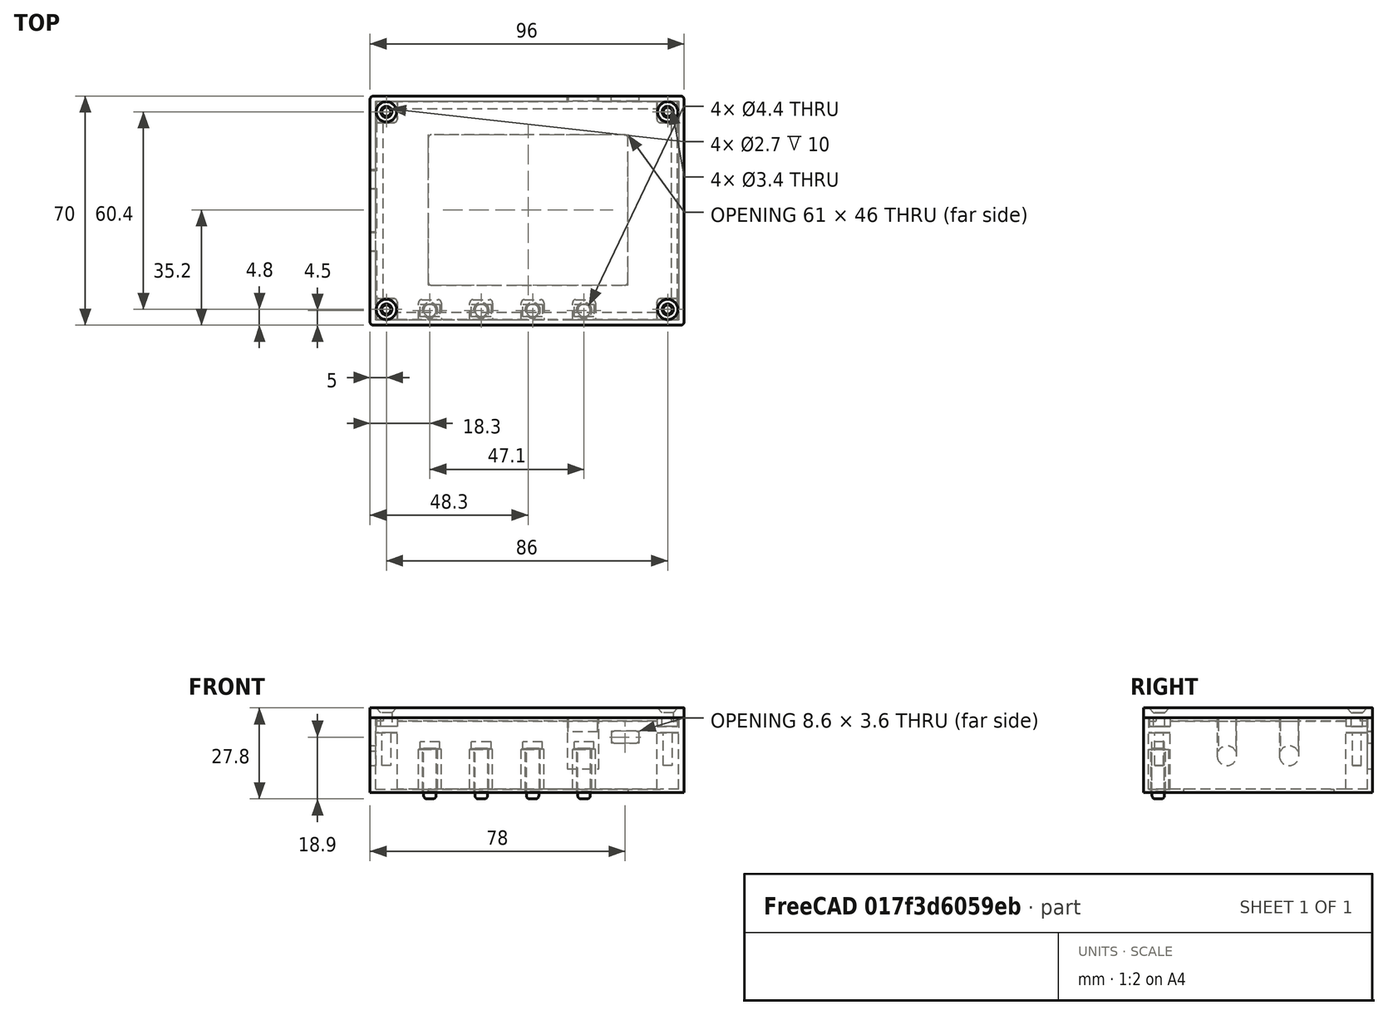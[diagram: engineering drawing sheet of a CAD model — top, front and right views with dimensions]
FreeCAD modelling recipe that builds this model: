
FCSTD DOCUMENT  (FreeCAD 0.18R16131 (Git))
Label: SigGen_Housing
License: All rights reserved
LicenseURL: http://en.wikipedia.org/wiki/All_rights_reserved
objects: Sketcher::SketchObject×35, PartDesign::Pad×18, PartDesign::Pocket×17, PartDesign::Fillet×10, PartDesign::Body×6, Mesh::Feature×3, PartDesign::Chamfer×2, Spreadsheet::Sheet×1
note: 123 computed .brp shape members not serialized (recipe doc carries the construction recipe); baked Part::Feature solids carry a one-line shape summary decoded from their .brp

FEATURE [Sketcher::SketchObject] Sketch
  MapMode = 5
  Support = -> [XY_Plane]
  expr: Constraints[11] = Constraints.OWidth / 2
  expr: Constraints[10] = Constraints.OLength / 2
  expr: Constraints.OWidth = Measures.B2
  expr: Constraints.OLength = Measures.A2
  sketch-geometry (4):
    g0: LineSegment StartX=-48 StartY=35 StartZ=0 EndX=48 EndY=35 EndZ=0
    g1: LineSegment StartX=48 StartY=35 StartZ=0 EndX=48 EndY=-35 EndZ=0
    g2: LineSegment StartX=48 StartY=-35 StartZ=0 EndX=-48 EndY=-35 EndZ=0
    g3: LineSegment StartX=-48 StartY=-35 StartZ=0 EndX=-48 EndY=35 EndZ=0
  constraints (12):
    c: Coincident(g0,g1)
    c: Coincident(g1,g2)
    c: Coincident(g2,g3)
    c: Coincident(g3,g0)
    c: Horizontal(g0)
    c: Horizontal(g2)
    c: Vertical(g1)
    c: Vertical(g3)
    c: DistanceX(g0,g0) = 96  'OLength'
    c: DistanceY(g3,g3) = 70  'OWidth'
    c: Distance(g-1,g3) = 48
    c: Distance(g-1,g0) = 35
FEATURE [Spreadsheet::Sheet] Spreadsheet  label="Measures"
  cells = A1=Lenght outer; B1=Width outer; C1=Height outer; D1=Length inner; E1=Width inner; F1=Height inner; G1=Length PCB; H1=Width PCB; I1=Height PCB; J1=Tolerance; K1=Length LCD; L1=Width LCD; A2=96; B2==E2 + 3; C2==1 + F2 + I2 + 3; D2==G2 + 2 * J2; E2==H2 + 2 * J2; F2==16.9 + J2; G2=92; H2=66.40000000000001; I2=1.6; J2=0.3; K2=61; L2=46
FEATURE [PartDesign::Pad] Pad
  Length = 22.8
  Length2 = 100
  Profile = -> Sketch
  Type = 0
  expr: Length = Measures.C2
FEATURE [Sketcher::SketchObject] Sketch001
  MapMode = 5
  Placement = pos=(0,0,22.8) rot=(0,0,1;0rad)
  Support = -> [Pad]
  expr: Constraints[11] = Constraints.ILength / 2
  expr: Constraints[10] = Constraints.IWidth / 2
  expr: Constraints.IWidth = Measures.E2
  expr: Constraints.ILength = Measures.D2
  sketch-geometry (4):
    g0: LineSegment StartX=-46.3 StartY=33.5 StartZ=0 EndX=46.3 EndY=33.5 EndZ=0
    g1: LineSegment StartX=46.3 StartY=33.5 StartZ=0 EndX=46.3 EndY=-33.5 EndZ=0
    g2: LineSegment StartX=46.3 StartY=-33.5 StartZ=0 EndX=-46.3 EndY=-33.5 EndZ=0
    g3: LineSegment StartX=-46.3 StartY=-33.5 StartZ=0 EndX=-46.3 EndY=33.5 EndZ=0
  constraints (12):
    c: Coincident(g0,g1)
    c: Coincident(g1,g2)
    c: Coincident(g2,g3)
    c: Coincident(g3,g0)
    c: Horizontal(g0)
    c: Horizontal(g2)
    c: Vertical(g1)
    c: Vertical(g3)
    c: DistanceX(g0,g0) = 92.6  'ILength'
    c: DistanceY(g3,g3) = 67  'IWidth'
    c: Distance(g-1,g0) = 33.5
    c: Distance(g-1,g3) = 46.3
FEATURE [PartDesign::Pocket] Pocket
  BaseFeature = -> Pad
  Length = 21.8
  Length2 = 100
  Profile = -> Sketch001
  Type = 0
  expr: Length = Measures.F2 + Measures.I2 + 3
FEATURE [Sketcher::SketchObject] Sketch002
  ExternalGeometry = -> [Pocket]
  MapMode = 5
  Placement = pos=(0,0,1) rot=(0,0,1;0rad)
  Support = -> [Pocket]
  expr: Constraints[39] = 6 + 2 * Measures.J2
  expr: Constraints[37] = 6 + 2 * Measures.J2
  expr: Constraints[35] = 6 + 2 * Measures.J2
  expr: Constraints[36] = 6 + 2 * Measures.J2
  expr: Constraints[34] = 6 + 2 * Measures.J2
  expr: Constraints[33] = 6 + 2 * Measures.J2
  expr: Constraints[38] = 6 + 2 * Measures.J2
  expr: Constraints[32] = 6 + 2 * Measures.J2
  sketch-geometry (16):
    g0: LineSegment StartX=-46.3 StartY=33.5 StartZ=0 EndX=-39.7 EndY=33.5 EndZ=0
    g1: LineSegment StartX=-39.7 StartY=33.5 StartZ=0 EndX=-39.7 EndY=26.9 EndZ=0
    g2: LineSegment StartX=-39.7 StartY=26.9 StartZ=0 EndX=-46.3 EndY=26.9 EndZ=0
    g3: LineSegment StartX=-46.3 StartY=26.9 StartZ=0 EndX=-46.3 EndY=33.5 EndZ=0
    g4: LineSegment StartX=39.7 StartY=33.5 StartZ=0 EndX=46.3 EndY=33.5 EndZ=0
    g5: LineSegment StartX=46.3 StartY=33.5 StartZ=0 EndX=46.3 EndY=26.9 EndZ=0
    g6: LineSegment StartX=46.3 StartY=26.9 StartZ=0 EndX=39.7 EndY=26.9 EndZ=0
    g7: LineSegment StartX=39.7 StartY=26.9 StartZ=0 EndX=39.7 EndY=33.5 EndZ=0
    g8: LineSegment StartX=39.7 StartY=-26.9 StartZ=0 EndX=46.3 EndY=-26.9 EndZ=0
    g9: LineSegment StartX=46.3 StartY=-26.9 StartZ=0 EndX=46.3 EndY=-33.5 EndZ=0
    g10: LineSegment StartX=46.3 StartY=-33.5 StartZ=0 EndX=39.7 EndY=-33.5 EndZ=0
    g11: LineSegment StartX=39.7 StartY=-33.5 StartZ=0 EndX=39.7 EndY=-26.9 EndZ=0
    g12: LineSegment StartX=-46.3 StartY=-26.9 StartZ=0 EndX=-39.7 EndY=-26.9 EndZ=0
    g13: LineSegment StartX=-39.7 StartY=-26.9 StartZ=0 EndX=-39.7 EndY=-33.5 EndZ=0
    g14: LineSegment StartX=-39.7 StartY=-33.5 StartZ=0 EndX=-46.3 EndY=-33.5 EndZ=0
    g15: LineSegment StartX=-46.3 StartY=-33.5 StartZ=0 EndX=-46.3 EndY=-26.9 EndZ=0
  constraints (44):
    c: Coincident(g0,g1)
    c: Coincident(g1,g2)
    c: Coincident(g2,g3)
    c: Coincident(g3,g0)
    c: Horizontal(g0)
    c: Horizontal(g2)
    c: Vertical(g1)
    c: Vertical(g3)
    c: Coincident(g4,g5)
    c: Coincident(g5,g6)
    c: Coincident(g6,g7)
    c: Coincident(g7,g4)
    c: Horizontal(g4)
    c: Horizontal(g6)
    c: Vertical(g5)
    c: Vertical(g7)
    c: Coincident(g8,g9)
    c: Coincident(g9,g10)
    c: Coincident(g10,g11)
    c: Coincident(g11,g8)
    c: Horizontal(g8)
    c: Horizontal(g10)
    c: Vertical(g9)
    c: Vertical(g11)
    c: Coincident(g12,g13)
    c: Coincident(g13,g14)
    c: Coincident(g14,g15)
    c: Coincident(g15,g12)
    c: Horizontal(g12)
    c: Horizontal(g14)
    c: Vertical(g13)
    c: Vertical(g15)
    c: DistanceX(g2,g2) = 6.6
    c: DistanceY(g1,g1) = 6.6
    c: DistanceY(g7,g7) = 6.6
    c: DistanceX(g6,g6) = 6.6
    c: DistanceX(g12,g12) = 6.6
    c: DistanceY(g13,g13) = 6.6
    c: DistanceX(g8,g8) = 6.6
    c: DistanceY(g11,g11) = 6.6
    c: Coincident(g14,g-4)
    c: Coincident(g9,g-3)
    c: Coincident(g4,g-3)
    c: Coincident(g-4,g0)
FEATURE [PartDesign::Pad] Pad001
  BaseFeature = -> Pocket
  Length = 17.2
  Length2 = 100
  Profile = -> Sketch002
  Type = 0
  expr: Length = Measures.F2
FEATURE [Sketcher::SketchObject] Sketch003
  ExternalGeometry = -> [Pad001]
  MapMode = 5
  Placement = pos=(0,0,1) rot=(0,0,1;0rad)
  Support = -> [Pad001]
  expr: Constraints[11] = 10 + Measures.J2
  expr: Constraints[10] = 15.8 + Measures.J2
  expr: Constraints[9] = Measures.K2
  expr: Constraints[8] = Measures.L2
  sketch-geometry (4):
    g0: LineSegment StartX=-30.2 StartY=23.2 StartZ=0 EndX=30.8 EndY=23.2 EndZ=0
    g1: LineSegment StartX=30.8 StartY=23.2 StartZ=0 EndX=30.8 EndY=-22.8 EndZ=0
    g2: LineSegment StartX=30.8 StartY=-22.8 StartZ=0 EndX=-30.2 EndY=-22.8 EndZ=0
    g3: LineSegment StartX=-30.2 StartY=-22.8 StartZ=0 EndX=-30.2 EndY=23.2 EndZ=0
  constraints (12):
    c: Coincident(g0,g1)
    c: Coincident(g1,g2)
    c: Coincident(g2,g3)
    c: Coincident(g3,g0)
    c: Horizontal(g0)
    c: Horizontal(g2)
    c: Vertical(g1)
    c: Vertical(g3)
    c: DistanceY(g3,g3) = 46
    c: DistanceX(g0,g0) = 61
    c: Distance(g0,g-3) = 16.1
    c: Distance(g0,g-4) = 10.3
FEATURE [PartDesign::Pocket] Pocket001
  BaseFeature = -> Pad001
  Length = 5
  Length2 = 100
  Profile = -> Sketch003
  Type = 1
FEATURE [Sketcher::SketchObject] Sketch004
  ExternalGeometry = -> [Pocket001]
  MapMode = 5
  Placement = pos=(0,0,18.2) rot=(0,0,1;0rad)
  Support = -> [Pocket001]
  expr: Constraints[2] = (6 + Measures.J2 * 2) / 2
  expr: Constraints[1] = (6 + Measures.J2 * 2) / 2
  sketch-geometry (1):
    g0: Circle CenterX=-43 CenterY=30.2 CenterZ=0 NormalX=0 NormalY=0 NormalZ=1 AngleXU=0 Radius=1.35
  constraints (3):
    c: Radius(g0) = 1.35
    c: Distance(g0,g-3) = 3.3
    c: Distance(g0,g-4) = 3.3
FEATURE [PartDesign::Pocket] Pocket002
  BaseFeature = -> Pocket001
  Length = 10
  Length2 = 100
  Profile = -> Sketch004
  Type = 0
FEATURE [Sketcher::SketchObject] Sketch005
  ExternalGeometry = -> [Pocket002]
  MapMode = 5
  Placement = pos=(0,0,18.2) rot=(0,0,1;0rad)
  Support = -> [Pocket002]
  expr: Constraints[2] = (6 + Measures.J2 * 2) / 2
  expr: Constraints[1] = (6 + Measures.J2 * 2) / 2
  sketch-geometry (1):
    g0: Circle CenterX=43 CenterY=30.2 CenterZ=0 NormalX=0 NormalY=0 NormalZ=1 AngleXU=0 Radius=1.35
  constraints (3):
    c: Radius(g0) = 1.35
    c: Distance(g0,g-4) = 3.3
    c: Distance(g0,g-3) = 3.3
FEATURE [PartDesign::Pocket] Pocket003
  BaseFeature = -> Pocket002
  Length = 10
  Length2 = 100
  Profile = -> Sketch005
  Type = 0
FEATURE [Sketcher::SketchObject] Sketch006
  ExternalGeometry = -> [Pocket003]
  MapMode = 5
  Placement = pos=(0,0,18.2) rot=(0,0,1;0rad)
  Support = -> [Pocket003]
  expr: Constraints[2] = (6 + Measures.J2 * 2) / 2
  expr: Constraints[1] = (6 + Measures.J2 * 2) / 2
  sketch-geometry (1):
    g0: Circle CenterX=-43 CenterY=-30.2 CenterZ=0 NormalX=0 NormalY=0 NormalZ=1 AngleXU=0 Radius=1.35
  constraints (3):
    c: Radius(g0) = 1.35
    c: Distance(g0,g-4) = 3.3
    c: Distance(g0,g-3) = 3.3
FEATURE [PartDesign::Pocket] Pocket004
  BaseFeature = -> Pocket003
  Length = 10
  Length2 = 100
  Profile = -> Sketch006
  Type = 0
FEATURE [Sketcher::SketchObject] Sketch007
  ExternalGeometry = -> [Pocket004]
  MapMode = 5
  Placement = pos=(0,0,18.2) rot=(0,0,1;0rad)
  Support = -> [Pocket004]
  expr: Constraints[2] = (6 + Measures.J2 * 2) / 2
  expr: Constraints[1] = (6 + Measures.J2 * 2) / 2
  sketch-geometry (1):
    g0: Circle CenterX=43 CenterY=-30.2 CenterZ=0 NormalX=0 NormalY=0 NormalZ=1 AngleXU=0 Radius=1.35
  constraints (3):
    c: Radius(g0) = 1.35
    c: Distance(g0,g-3) = 3.3
    c: Distance(g0,g-4) = 3.3
FEATURE [PartDesign::Pocket] Pocket005
  BaseFeature = -> Pocket004
  Length = 10
  Length2 = 100
  Profile = -> Sketch007
  Type = 0
FEATURE [Sketcher::SketchObject] Sketch008
  ExternalGeometry = -> [Pocket005]
  MapMode = 5
  Placement = pos=(-46.3,0,0) rot=(0.57735,0.57735,0.57735;2.0944rad)
  Support = -> [Pocket005]
  sketch-geometry (8):
    g0: LineSegment StartX=-12.5 StartY=22.8 StartZ=0 EndX=-6.5 EndY=22.8 EndZ=0
    g1: LineSegment StartX=-6.5 StartY=22.8 StartZ=0 EndX=-6.5 EndY=11.2 EndZ=0
    g2: LineSegment StartX=-12.5 StartY=11.2 StartZ=0 EndX=-12.5 EndY=22.8 EndZ=0
    g3: LineSegment StartX=6.5 StartY=22.8 StartZ=0 EndX=12.5 EndY=22.8 EndZ=0
    g4: LineSegment StartX=12.5 StartY=22.8 StartZ=0 EndX=12.5 EndY=11.2 EndZ=0
    g5: LineSegment StartX=6.5 StartY=11.2 StartZ=0 EndX=6.5 EndY=22.8 EndZ=0
    g6: ArcOfCircle CenterX=9.5 CenterY=11.2 CenterZ=0 NormalX=0 NormalY=0 NormalZ=1 AngleXU=0 Radius=3 StartAngle=3.14159 EndAngle=6.28319
    g7: ArcOfCircle CenterX=-9.5 CenterY=11.2 CenterZ=0 NormalX=0 NormalY=0 NormalZ=1 AngleXU=0 Radius=3 StartAngle=3.14159 EndAngle=6.28319
  constraints (26):
    c: Coincident(g0,g1)
    c: Coincident(g2,g0)
    c: Horizontal(g0)
    c: Vertical(g1)
    c: Vertical(g2)
    c: Coincident(g3,g4)
    c: Coincident(g5,g3)
    c: Horizontal(g3)
    c: Vertical(g4)
    c: Vertical(g5)
    c: DistanceX(g2,g1) = 6
    c: DistanceX(g5,g4) = 6
    c: PointOnObject(g3,g-8)
    c: PointOnObject(g0,g-8)
    c: DistanceY(g5,g5) = 11.6
    c: DistanceY(g1,g1) = 11.6
    c: DistanceY(g4,g4) = 11.6
    c: DistanceY(g2,g2) = 11.6
    c: Coincident(g6,g4)
    c: Coincident(g6,g5)
    c: Coincident(g7,g1)
    c: Coincident(g7,g2)
    c: Distance(g7,g6) = 19
    c: Distance(g6,g-9) = 24
    c: Distance(g7,g0) = 11.6
    c: Distance(g6,g3) = 11.6
FEATURE [PartDesign::Pocket] Pocket006
  BaseFeature = -> Pocket005
  Length = 5
  Length2 = 100
  Profile = -> Sketch008
  Type = 1
FEATURE [Sketcher::SketchObject] Sketch009
  ExternalGeometry = -> [Pocket006]
  MapMode = 5
  Placement = pos=(0,0,1) rot=(0,0,1;0rad)
  Support = -> [Pocket006]
  expr: Constraints[47] = 16.3 + Measures.J2 - 7 / 2
  expr: Constraints[39] = 6 + Measures.J2
  expr: Constraints[38] = 6 + Measures.J2
  expr: Constraints[37] = 6 + Measures.J2
  expr: Constraints[36] = 6 + Measures.J2
  sketch-geometry (16):
    g0: LineSegment StartX=-33.2 StartY=-27.2 StartZ=0 EndX=-26.2 EndY=-27.2 EndZ=0
    g1: LineSegment StartX=-26.2 StartY=-27.2 StartZ=0 EndX=-26.2 EndY=-33.5 EndZ=0
    g2: LineSegment StartX=-26.2 StartY=-33.5 StartZ=0 EndX=-33.2 EndY=-33.5 EndZ=0
    g3: LineSegment StartX=-33.2 StartY=-33.5 StartZ=0 EndX=-33.2 EndY=-27.2 EndZ=0
    g4: LineSegment StartX=-17.5 StartY=-27.2 StartZ=0 EndX=-10.5 EndY=-27.2 EndZ=0
    g5: LineSegment StartX=-10.5 StartY=-27.2 StartZ=0 EndX=-10.5 EndY=-33.5 EndZ=0
    g6: LineSegment StartX=-10.5 StartY=-33.5 StartZ=0 EndX=-17.5 EndY=-33.5 EndZ=0
    g7: LineSegment StartX=-17.5 StartY=-33.5 StartZ=0 EndX=-17.5 EndY=-27.2 EndZ=0
    g8: LineSegment StartX=-1.8 StartY=-27.2 StartZ=0 EndX=5.2 EndY=-27.2 EndZ=0
    g9: LineSegment StartX=5.2 StartY=-27.2 StartZ=0 EndX=5.2 EndY=-33.5 EndZ=0
    g10: LineSegment StartX=5.2 StartY=-33.5 StartZ=0 EndX=-1.8 EndY=-33.5 EndZ=0
    g11: LineSegment StartX=-1.8 StartY=-33.5 StartZ=0 EndX=-1.8 EndY=-27.2 EndZ=0
    g12: LineSegment StartX=13.9 StartY=-27.2 StartZ=0 EndX=20.9 EndY=-27.2 EndZ=0
    g13: LineSegment StartX=20.9 StartY=-27.2 StartZ=0 EndX=20.9 EndY=-33.5 EndZ=0
    g14: LineSegment StartX=20.9 StartY=-33.5 StartZ=0 EndX=13.9 EndY=-33.5 EndZ=0
    g15: LineSegment StartX=13.9 StartY=-33.5 StartZ=0 EndX=13.9 EndY=-27.2 EndZ=0
  constraints (48):
    c: Coincident(g0,g1)
    c: Coincident(g1,g2)
    c: Coincident(g2,g3)
    c: Coincident(g3,g0)
    c: Horizontal(g0)
    c: Horizontal(g2)
    c: Vertical(g1)
    c: Vertical(g3)
    c: Coincident(g4,g5)
    c: Coincident(g5,g6)
    c: Coincident(g6,g7)
    c: Coincident(g7,g4)
    c: Horizontal(g4)
    c: Horizontal(g6)
    c: Vertical(g5)
    c: Vertical(g7)
    c: Coincident(g8,g9)
    c: Coincident(g9,g10)
    c: Coincident(g10,g11)
    c: Coincident(g11,g8)
    c: Horizontal(g8)
    c: Horizontal(g10)
    c: Vertical(g9)
    c: Vertical(g11)
    c: Coincident(g12,g13)
    c: Coincident(g13,g14)
    c: Coincident(g14,g15)
    c: Coincident(g15,g12)
    c: Horizontal(g12)
    c: Horizontal(g14)
    c: Vertical(g13)
    c: Vertical(g15)
    c: DistanceX(g0,g0) = 7
    c: DistanceX(g4,g4) = 7
    c: DistanceX(g8,g8) = 7
    c: DistanceX(g12,g12) = 7
    c: DistanceY(g1,g1) = 6.3
    c: DistanceY(g5,g5) = 6.3
    c: DistanceY(g9,g9) = 6.3
    c: DistanceY(g13,g13) = 6.3
    c: PointOnObject(g1,g-3)
    c: PointOnObject(g5,g-3)
    c: PointOnObject(g9,g-3)
    c: PointOnObject(g13,g-3)
    c: Distance(g0,g7) = 15.7
    c: Distance(g4,g11) = 15.7
    c: Distance(g8,g15) = 15.7
    c: Distance(g0,g-4) = 13.1
FEATURE [PartDesign::Pad] Pad002
  BaseFeature = -> Pocket006
  Length = 12.2
  Length2 = 100
  Profile = -> Sketch009
  Type = 0
  expr: Length = Measures.F2 - 2.7 - 2 - Measures.J2
FEATURE [Sketcher::SketchObject] Sketch010
  ExternalGeometry = -> [Pad002]
  MapMode = 5
  Placement = pos=(0,0,13.2) rot=(0,0,1;0rad)
  Support = -> [Pad002]
  expr: Constraints[0] = 2.7 + Measures.J2
  sketch-geometry (1):
    g0: Circle CenterX=-29.7 CenterY=-30.5 CenterZ=0 NormalX=0 NormalY=0 NormalZ=1 AngleXU=0 Radius=2.2
  constraints (3):
    c: Distance(g0,g-3) = 3
    c: Radius(g0) = 2.2
    c: Distance(g0,g-4) = 3.5
FEATURE [PartDesign::Pocket] Pocket007
  BaseFeature = -> Pad002
  Length = 5
  Length2 = 100
  Profile = -> Sketch010
  Type = 1
FEATURE [Sketcher::SketchObject] Sketch011
  ExternalGeometry = -> [Pocket007]
  MapMode = 5
  Placement = pos=(0,0,13.2) rot=(0,0,1;0rad)
  Support = -> [Pocket007]
  expr: Constraints[0] = 2.7 + Measures.J2
  sketch-geometry (1):
    g0: Circle CenterX=-14 CenterY=-30.5 CenterZ=0 NormalX=0 NormalY=0 NormalZ=1 AngleXU=0 Radius=2.2
  constraints (3):
    c: Distance(g0,g-3) = 3
    c: Radius(g0) = 2.2
    c: Distance(g0,g-4) = 3.5
FEATURE [PartDesign::Pocket] Pocket008
  BaseFeature = -> Pocket007
  Length = 5
  Length2 = 100
  Profile = -> Sketch011
  Type = 1
FEATURE [Sketcher::SketchObject] Sketch012
  ExternalGeometry = -> [Pocket008]
  MapMode = 5
  Placement = pos=(0,0,13.2) rot=(0,0,1;0rad)
  Support = -> [Pocket008]
  expr: Constraints[1] = 2.7 + Measures.J2
  sketch-geometry (1):
    g0: Circle CenterX=1.7 CenterY=-30.5 CenterZ=0 NormalX=0 NormalY=0 NormalZ=1 AngleXU=0 Radius=2.2
  constraints (3):
    c: Radius(g0) = 2.2
    c: Distance(g0,g-3) = 3
    c: Distance(g0,g-4) = 3.5
FEATURE [PartDesign::Pocket] Pocket009
  BaseFeature = -> Pocket008
  Length = 5
  Length2 = 100
  Profile = -> Sketch012
  Type = 1
FEATURE [Sketcher::SketchObject] Sketch013
  ExternalGeometry = -> [Pocket009]
  MapMode = 5
  Placement = pos=(0,0,13.2) rot=(0,0,1;0rad)
  Support = -> [Pocket009]
  expr: Constraints[0] = 2.7 + Measures.J2
  sketch-geometry (1):
    g0: Circle CenterX=17.4 CenterY=-30.5 CenterZ=0 NormalX=0 NormalY=0 NormalZ=1 AngleXU=0 Radius=2.2
  constraints (3):
    c: Distance(g0,g-3) = 3
    c: Radius(g0) = 2.2
    c: Distance(g0,g-4) = 3.5
FEATURE [PartDesign::Pocket] Pocket010
  BaseFeature = -> Pocket009
  Length = 5
  Length2 = 100
  Profile = -> Sketch013
  Type = 1
FEATURE [Sketcher::SketchObject] Sketch014
  ExternalGeometry = -> [Pocket010]
  MapMode = 5
  Placement = pos=(0,33.5,0) rot=(1,0,0;1.5708rad)
  Support = -> [Pocket010]
  expr: Constraints[11] = 24.1 + Measures.J2
  expr: Constraints[9] = Measures.F2 - 11
  sketch-geometry (4):
    g0: LineSegment StartX=12.3 StartY=22.8 StartZ=0 EndX=21.9 EndY=22.8 EndZ=0
    g1: LineSegment StartX=21.9 StartY=22.8 StartZ=0 EndX=21.9 EndY=7.2 EndZ=0
    g2: LineSegment StartX=21.9 StartY=7.2 StartZ=0 EndX=12.3 EndY=7.2 EndZ=0
    g3: LineSegment StartX=12.3 StartY=7.2 StartZ=0 EndX=12.3 EndY=22.8 EndZ=0
  constraints (12):
    c: Coincident(g0,g1)
    c: Coincident(g1,g2)
    c: Coincident(g2,g3)
    c: Coincident(g3,g0)
    c: Horizontal(g0)
    c: Horizontal(g2)
    c: Vertical(g1)
    c: Vertical(g3)
    c: DistanceX(g2,g2) = 9.6
    c: Distance(g1,g-4) = 6.2
    c: PointOnObject(g0,g-5)
    c: Distance(g0,g-3) = 24.4
FEATURE [PartDesign::Pocket] Pocket011
  BaseFeature = -> Pocket010
  Length = 5
  Length2 = 100
  Profile = -> Sketch014
  Type = 1
FEATURE [Sketcher::SketchObject] Sketch015
  ExternalGeometry = -> [Pocket011]
  MapMode = 5
  Placement = pos=(0,33.5,0) rot=(1,0,0;1.5708rad)
  Support = -> [Pocket011]
  expr: Constraints[11] = Measures.F2 - 3 - Measures.J2 + 0.2
  expr: Constraints[9] = 3 + 2 * Measures.J2
  expr: Constraints[8] = 8 + 2 * Measures.J2
  sketch-geometry (4):
    g0: LineSegment StartX=25.7 StartY=18.7 StartZ=0 EndX=34.3 EndY=18.7 EndZ=0
    g1: LineSegment StartX=34.3 StartY=18.7 StartZ=0 EndX=34.3 EndY=15.1 EndZ=0
    g2: LineSegment StartX=34.3 StartY=15.1 StartZ=0 EndX=25.7 EndY=15.1 EndZ=0
    g3: LineSegment StartX=25.7 StartY=15.1 StartZ=0 EndX=25.7 EndY=18.7 EndZ=0
  constraints (12):
    c: Coincident(g0,g1)
    c: Coincident(g1,g2)
    c: Coincident(g2,g3)
    c: Coincident(g3,g0)
    c: Horizontal(g0)
    c: Horizontal(g2)
    c: Vertical(g1)
    c: Vertical(g3)
    c: DistanceX(g2,g2) = 8.6
    c: DistanceY(g1,g1) = 3.6
    c: Distance(g0,g-4) = 12
    c: Distance(g1,g-3) = 14.1
FEATURE [PartDesign::Pocket] Pocket012
  BaseFeature = -> Pocket011
  Length = 5
  Length2 = 100
  Profile = -> Sketch015
  Type = 1
FEATURE [PartDesign::Fillet] Fillet
  Base = -> Pocket012 [Edge3,Edge2,Edge33,Edge34]
  BaseFeature = -> Pocket012
  Radius = 1
FEATURE [PartDesign::Fillet] Fillet001
  Base = -> Fillet [Edge176,Edge177,Edge193,Edge192,Edge191,Edge190,Edge189,Edge188,Edge187,Edge186,Edge185,Edge181]
  BaseFeature = -> Fillet
  Radius = 1
FEATURE [PartDesign::Chamfer] Chamfer
  Base = -> Fillet001 [Edge149,Edge150,Edge148,Edge41]
  BaseFeature = -> Fillet001
  Size = 0.2
FEATURE [PartDesign::Fillet] Fillet002
  Base = -> Chamfer [Edge202,Edge203,Edge207,Edge205]
  BaseFeature = -> Chamfer
  Radius = 1
FEATURE [PartDesign::Fillet] Fillet003
  Base = -> Fillet002 [Edge99,Edge95,Edge94,Edge97]
  BaseFeature = -> Fillet002
  Radius = 1
FEATURE [PartDesign::Body] Body  label="Housing"
  Group = -> [Sketch,Pad,Sketch001,Pocket,Sketch002,Pad001,Sketch003,Pocket001,Sketch004,Pocket002,Sketch005,Pocket003,Sketch006,Pocket004,Sketch007,Pocket005,Sketch008,Pocket006,Sketch009,Pad002,Sketch010,Pocket007,Sketch011,Pocket008,Sketch012,Pocket009,Sketch013,Pocket010,Sketch014,Pocket011,Sketch015,Pocket012,Fillet,Fillet001,Chamfer,Fillet002,Fillet003]
  Origin = -> Origin
  Tip = -> Fillet003
FEATURE [Sketcher::SketchObject] Sketch016
  AttachmentOffset = pos=(0,0,22.8) rot=(0,0,1;0rad)
  MapMode = 5
  Placement = pos=(0,0,22.8) rot=(0,0,1;0rad)
  Support = -> [XY_Plane001]
  expr: Constraints[11] = Constraints.COWidth / 2
  expr: Constraints[10] = Constraints.COLenght / 2
  expr: Constraints.COLenght = Measures.A2
  expr: Constraints.COWidth = Measures.B2
  expr: AttachmentOffset.Base.z = Measures.C2
  sketch-geometry (4):
    g0: LineSegment StartX=-48 StartY=35 StartZ=0 EndX=48 EndY=35 EndZ=0
    g1: LineSegment StartX=48 StartY=35 StartZ=0 EndX=48 EndY=-35 EndZ=0
    g2: LineSegment StartX=48 StartY=-35 StartZ=0 EndX=-48 EndY=-35 EndZ=0
    g3: LineSegment StartX=-48 StartY=-35 StartZ=0 EndX=-48 EndY=35 EndZ=0
  constraints (12):
    c: Coincident(g0,g1)
    c: Coincident(g1,g2)
    c: Coincident(g2,g3)
    c: Coincident(g3,g0)
    c: Horizontal(g0)
    c: Horizontal(g2)
    c: Vertical(g1)
    c: Vertical(g3)
    c: DistanceY(g3,g3) = 70  'COWidth'
    c: DistanceX(g0,g0) = 96  'COLenght'
    c: Distance(g-1,g3) = 48
    c: Distance(g-1,g0) = 35
FEATURE [PartDesign::Pad] Pad003
  Length = 3
  Length2 = 100
  Profile = -> Sketch016
  Type = 0
FEATURE [Sketcher::SketchObject] Sketch017
  ExternalGeometry = -> [Pad003]
  MapMode = 5
  Placement = pos=(0,0,22.8) rot=(1,0,0;3.14159rad)
  Support = -> [Pad003]
  expr: Constraints[47] = 1.7 + Measures.J2
  expr: Constraints[46] = 1.5 + Measures.J2
  expr: Constraints[45] = 1.5 + Measures.J2
  expr: Constraints[44] = 1.7 + Measures.J2
  expr: Constraints[43] = 1.7 + Measures.J2
  expr: Constraints[42] = 1.5 + Measures.J2
  expr: Constraints[41] = 1.5 + Measures.J2
  expr: Constraints[40] = 1.7 + Measures.J2
  sketch-geometry (16):
    g0: LineSegment StartX=-46 StartY=33.2 StartZ=0 EndX=-39.7 EndY=33.2 EndZ=0
    g1: LineSegment StartX=-39.7 StartY=33.2 StartZ=0 EndX=-39.7 EndY=26.9 EndZ=0
    g2: LineSegment StartX=-39.7 StartY=26.9 StartZ=0 EndX=-46 EndY=26.9 EndZ=0
    g3: LineSegment StartX=-46 StartY=26.9 StartZ=0 EndX=-46 EndY=33.2 EndZ=0
    g4: LineSegment StartX=39.7 StartY=33.2 StartZ=0 EndX=46 EndY=33.2 EndZ=0
    g5: LineSegment StartX=46 StartY=33.2 StartZ=0 EndX=46 EndY=26.9 EndZ=0
    g6: LineSegment StartX=46 StartY=26.9 StartZ=0 EndX=39.7 EndY=26.9 EndZ=0
    g7: LineSegment StartX=39.7 StartY=26.9 StartZ=0 EndX=39.7 EndY=33.2 EndZ=0
    g8: LineSegment StartX=39.7 StartY=-26.9 StartZ=0 EndX=46 EndY=-26.9 EndZ=0
    g9: LineSegment StartX=46 StartY=-26.9 StartZ=0 EndX=46 EndY=-33.2 EndZ=0
    g10: LineSegment StartX=46 StartY=-33.2 StartZ=0 EndX=39.7 EndY=-33.2 EndZ=0
    g11: LineSegment StartX=39.7 StartY=-33.2 StartZ=0 EndX=39.7 EndY=-26.9 EndZ=0
    g12: LineSegment StartX=-46 StartY=-26.9 StartZ=0 EndX=-39.7 EndY=-26.9 EndZ=0
    g13: LineSegment StartX=-39.7 StartY=-26.9 StartZ=0 EndX=-39.7 EndY=-33.2 EndZ=0
    g14: LineSegment StartX=-39.7 StartY=-33.2 StartZ=0 EndX=-46 EndY=-33.2 EndZ=0
    g15: LineSegment StartX=-46 StartY=-33.2 StartZ=0 EndX=-46 EndY=-26.9 EndZ=0
  constraints (48):
    c: Coincident(g0,g1)
    c: Coincident(g1,g2)
    c: Coincident(g2,g3)
    c: Coincident(g3,g0)
    c: Horizontal(g0)
    c: Horizontal(g2)
    c: Vertical(g1)
    c: Vertical(g3)
    c: Coincident(g4,g5)
    c: Coincident(g5,g6)
    c: Coincident(g6,g7)
    c: Coincident(g7,g4)
    c: Horizontal(g4)
    c: Horizontal(g6)
    c: Vertical(g5)
    c: Vertical(g7)
    c: Coincident(g8,g9)
    c: Coincident(g9,g10)
    c: Coincident(g10,g11)
    c: Coincident(g11,g8)
    c: Horizontal(g8)
    c: Horizontal(g10)
    c: Vertical(g9)
    c: Vertical(g11)
    c: Coincident(g12,g13)
    c: Coincident(g13,g14)
    c: Coincident(g14,g15)
    c: Coincident(g15,g12)
    c: Horizontal(g12)
    c: Horizontal(g14)
    c: Vertical(g13)
    c: Vertical(g15)
    c: DistanceX(g2,g2) = 6.3
    c: DistanceX(g6,g6) = 6.3
    c: DistanceX(g8,g8) = 6.3
    c: DistanceX(g12,g12) = 6.3
    c: DistanceY(g13,g13) = 6.3
    c: DistanceY(g3,g3) = 6.3
    c: DistanceY(g5,g5) = 6.3
    c: DistanceY(g9,g9) = 6.3
    c: Distance(g14,g-4) = 2
    c: Distance(g14,g-5) = 1.8
    c: Distance(g9,g-5) = 1.8
    c: Distance(g9,g-6) = 2
    c: Distance(g4,g-6) = 2
    c: Distance(g4,g-3) = 1.8
    c: Distance(g0,g-3) = 1.8
    c: Distance(g0,g-4) = 2
FEATURE [PartDesign::Pad] Pad004
  BaseFeature = -> Pad003
  Length = 2.7
  Length2 = 100
  Profile = -> Sketch017
  Type = 0
FEATURE [Sketcher::SketchObject] Sketch018
  ExternalGeometry = -> [Pad004]
  MapMode = 5
  Placement = pos=(0,0,25.8) rot=(0,0,1;0rad)
  Support = -> [Pad004]
  sketch-geometry (4):
    g0: Circle CenterX=-43 CenterY=30.2 CenterZ=0 NormalX=0 NormalY=0 NormalZ=1 AngleXU=0 Radius=1.7
    g1: Circle CenterX=43 CenterY=30.2 CenterZ=0 NormalX=0 NormalY=0 NormalZ=1 AngleXU=0 Radius=1.7
    g2: Circle CenterX=43 CenterY=-30.2 CenterZ=0 NormalX=0 NormalY=0 NormalZ=1 AngleXU=0 Radius=1.7
    g3: Circle CenterX=-43 CenterY=-30.2 CenterZ=0 NormalX=0 NormalY=0 NormalZ=1 AngleXU=0 Radius=1.7
  constraints (12):
    c: Radius(g0) = 1.7
    c: Equal(g0,g3)
    c: Equal(g0,g2)
    c: Equal(g0,g1)
    c: Distance(g0,g-3) = 5
    c: Distance(g0,g-4) = 4.8
    c: Distance(g1,g-5) = 5
    c: Distance(g1,g-4) = 4.8
    c: Distance(g2,g-6) = 4.8
    c: Distance(g2,g-5) = 5
    c: Distance(g3,g-3) = 5
    c: Distance(g3,g-6) = 4.8
FEATURE [PartDesign::Pocket] Pocket013
  BaseFeature = -> Pad004
  Length = 5
  Length2 = 100
  Profile = -> Sketch018
  Type = 1
FEATURE [Sketcher::SketchObject] Sketch019
  ExternalGeometry = -> [Pocket013]
  MapMode = 5
  Placement = pos=(0,0,22.8) rot=(1,0,0;3.14159rad)
  Support = -> [Pocket013]
  sketch-geometry (16):
    g0: LineSegment StartX=39.7 StartY=-33.2 StartZ=0 EndX=-39.7 EndY=-33.2 EndZ=0
    g1: LineSegment StartX=-39.7 StartY=-33.2 StartZ=0 EndX=-39.7 EndY=-31.2 EndZ=0
    g2: LineSegment StartX=-39.7 StartY=-31.2 StartZ=0 EndX=39.7 EndY=-31.2 EndZ=0
    g3: LineSegment StartX=39.7 StartY=-31.2 StartZ=0 EndX=39.7 EndY=-33.2 EndZ=0
    g4: LineSegment StartX=-44 StartY=-26.9 StartZ=0 EndX=-46 EndY=-26.9 EndZ=0
    g5: LineSegment StartX=-46 StartY=-26.9 StartZ=0 EndX=-46 EndY=26.9 EndZ=0
    g6: LineSegment StartX=-46 StartY=26.9 StartZ=0 EndX=-44 EndY=26.9 EndZ=0
    g7: LineSegment StartX=-44 StartY=26.9 StartZ=0 EndX=-44 EndY=-26.9 EndZ=0
    g8: LineSegment StartX=39.7 StartY=31.2 StartZ=0 EndX=-39.7 EndY=31.2 EndZ=0
    g9: LineSegment StartX=-39.7 StartY=31.2 StartZ=0 EndX=-39.7 EndY=33.2 EndZ=0
    g10: LineSegment StartX=-39.7 StartY=33.2 StartZ=0 EndX=39.7 EndY=33.2 EndZ=0
    g11: LineSegment StartX=39.7 StartY=33.2 StartZ=0 EndX=39.7 EndY=31.2 EndZ=0
    g12: LineSegment StartX=46 StartY=-26.9 StartZ=0 EndX=44 EndY=-26.9 EndZ=0
    g13: LineSegment StartX=44 StartY=-26.9 StartZ=0 EndX=44 EndY=26.9 EndZ=0
    g14: LineSegment StartX=44 StartY=26.9 StartZ=0 EndX=46 EndY=26.9 EndZ=0
    g15: LineSegment StartX=46 StartY=26.9 StartZ=0 EndX=46 EndY=-26.9 EndZ=0
  constraints (44):
    c: Coincident(g0,g1)
    c: Coincident(g1,g2)
    c: Coincident(g2,g3)
    c: Coincident(g3,g0)
    c: Horizontal(g0)
    c: Horizontal(g2)
    c: Vertical(g1)
    c: Vertical(g3)
    c: DistanceY(g1,g1) = 2
    c: Coincident(g0,g-9)
    c: PointOnObject(g1,g-4)
    c: Coincident(g4,g5)
    c: Coincident(g5,g6)
    c: Coincident(g6,g7)
    c: Coincident(g7,g4)
    c: Horizontal(g4)
    c: Horizontal(g6)
    c: Vertical(g5)
    c: Vertical(g7)
    c: DistanceX(g6,g6) = 2
    c: Coincident(g4,g-5)
    c: PointOnObject(g6,g-6)
    c: Coincident(g8,g9)
    c: Coincident(g9,g10)
    c: Coincident(g10,g11)
    c: Coincident(g11,g8)
    c: Horizontal(g8)
    c: Horizontal(g10)
    c: Vertical(g9)
    c: Vertical(g11)
    c: DistanceY(g11,g11) = 2
    c: Coincident(g9,g-3)
    c: PointOnObject(g8,g-8)
    c: Coincident(g12,g13)
    c: Coincident(g13,g14)
    c: Coincident(g14,g15)
    c: Coincident(g15,g12)
    c: Horizontal(g12)
    c: Horizontal(g14)
    c: Vertical(g13)
    c: Vertical(g15)
    c: DistanceX(g12,g12) = 2
    c: Coincident(g12,g-10)
    c: PointOnObject(g13,g-7)
FEATURE [PartDesign::Pad] Pad005
  BaseFeature = -> Pocket013
  Length = 1
  Length2 = 100
  Profile = -> Sketch019
  Type = 0
FEATURE [Sketcher::SketchObject] Sketch020
  ExternalGeometry = -> [Pad005]
  MapMode = 5
  Placement = pos=(0,0,22.8) rot=(1,0,0;3.14159rad)
  Support = -> [Pad005]
  expr: Constraints[8] = 1.5 + Measures.J2
  expr: Constraints[11] = 26.1 + Measures.J2
  expr: Constraints[10] = 9.6 - Measures.J2 * 2
  sketch-geometry (4):
    g0: LineSegment StartX=12.6 StartY=-33.2 StartZ=0 EndX=21.6 EndY=-33.2 EndZ=0
    g1: LineSegment StartX=21.6 StartY=-33.2 StartZ=0 EndX=21.6 EndY=-35 EndZ=0
    g2: LineSegment StartX=21.6 StartY=-35 StartZ=0 EndX=12.6 EndY=-35 EndZ=0
    g3: LineSegment StartX=12.6 StartY=-35 StartZ=0 EndX=12.6 EndY=-33.2 EndZ=0
  constraints (12):
    c: Coincident(g0,g1)
    c: Coincident(g1,g2)
    c: Coincident(g2,g3)
    c: Coincident(g3,g0)
    c: Horizontal(g0)
    c: Horizontal(g2)
    c: Vertical(g1)
    c: Vertical(g3)
    c: DistanceY(g1,g1) = 1.8
    c: PointOnObject(g1,g-3)
    c: DistanceX(g0,g0) = 9
    c: Distance(g-3,g1) = 26.4
FEATURE [PartDesign::Pad] Pad006
  BaseFeature = -> Pad005
  Length = 4.3
  Length2 = 100
  Profile = -> Sketch020
  Type = 0
  expr: Length = 4.6 - Measures.J2
FEATURE [Sketcher::SketchObject] Sketch021
  ExternalGeometry = -> [Pad006]
  MapMode = 5
  Placement = pos=(0,0,18.5) rot=(1,0,0;3.14159rad)
  Support = -> [Pad006]
  expr: Constraints[8] = Measures.J2
  sketch-geometry (4):
    g0: LineSegment StartX=12.6 StartY=-33.2 StartZ=0 EndX=21.6 EndY=-33.2 EndZ=0
    g1: LineSegment StartX=21.6 StartY=-33.2 StartZ=0 EndX=21.6 EndY=-33.5 EndZ=0
    g2: LineSegment StartX=21.6 StartY=-33.5 StartZ=0 EndX=12.6 EndY=-33.5 EndZ=0
    g3: LineSegment StartX=12.6 StartY=-33.5 StartZ=0 EndX=12.6 EndY=-33.2 EndZ=0
  constraints (11):
    c: Coincident(g0,g1)
    c: Coincident(g1,g2)
    c: Coincident(g2,g3)
    c: Coincident(g3,g0)
    c: Horizontal(g0)
    c: Horizontal(g2)
    c: Vertical(g1)
    c: Vertical(g3)
    c: DistanceY(g1,g1) = 0.3
    c: Coincident(g0,g-3)
    c: PointOnObject(g2,g-4)
FEATURE [PartDesign::Pocket] Pocket014
  BaseFeature = -> Pad006
  Length = 3.3
  Length2 = 100
  Profile = -> Sketch021
  Type = 0
FEATURE [Sketcher::SketchObject] Sketch022
  ExternalGeometry = -> [Pocket014]
  MapMode = 5
  Placement = pos=(0,0,22.8) rot=(1,0,0;3.14159rad)
  Support = -> [Pocket014]
  expr: Constraints[20] = 1.7 + Measures.J2
  expr: Constraints[19] = 6 - 2 * Measures.J2
  expr: Constraints[17] = 1.7 + Measures.J2
  expr: Constraints[16] = 6 - 2 * Measures.J2
  sketch-geometry (8):
    g0: LineSegment StartX=-48 StartY=12.2 StartZ=0 EndX=-46 EndY=12.2 EndZ=0
    g1: LineSegment StartX=-46 StartY=12.2 StartZ=0 EndX=-46 EndY=6.8 EndZ=0
    g2: LineSegment StartX=-46 StartY=6.8 StartZ=0 EndX=-48 EndY=6.8 EndZ=0
    g3: LineSegment StartX=-48 StartY=6.8 StartZ=0 EndX=-48 EndY=12.2 EndZ=0
    g4: LineSegment StartX=-48 StartY=-6.8 StartZ=0 EndX=-46 EndY=-6.8 EndZ=0
    g5: LineSegment StartX=-46 StartY=-6.8 StartZ=0 EndX=-46 EndY=-12.2 EndZ=0
    g6: LineSegment StartX=-46 StartY=-12.2 StartZ=0 EndX=-48 EndY=-12.2 EndZ=0
    g7: LineSegment StartX=-48 StartY=-12.2 StartZ=0 EndX=-48 EndY=-6.8 EndZ=0
  constraints (24):
    c: Coincident(g0,g1)
    c: Coincident(g1,g2)
    c: Coincident(g2,g3)
    c: Coincident(g3,g0)
    c: Horizontal(g0)
    c: Horizontal(g2)
    c: Vertical(g1)
    c: Vertical(g3)
    c: Coincident(g4,g5)
    c: Coincident(g5,g6)
    c: Coincident(g6,g7)
    c: Coincident(g7,g4)
    c: Horizontal(g4)
    c: Horizontal(g6)
    c: Vertical(g5)
    c: Vertical(g7)
    c: DistanceY(g1,g1) = 5.4
    c: DistanceX(g2,g2) = 2
    c: PointOnObject(g2,g-3)
    c: DistanceY(g5,g5) = 5.4
    c: DistanceX(g4,g4) = 2
    c: PointOnObject(g6,g-3)
    c: Distance(g-3,g6) = 22.8
    c: Distance(g0,g4) = 19
FEATURE [PartDesign::Pad] Pad007
  BaseFeature = -> Pocket014
  Length = 1
  Length2 = 100
  Profile = -> Sketch022
  Type = 0
FEATURE [Sketcher::SketchObject] Sketch023
  ExternalGeometry = -> [Pad007]
  MapMode = 5
  Placement = pos=(0,0,21.8) rot=(1,0,0;3.14159rad)
  Support = -> [Pad007]
  sketch-geometry (4):
    g0: LineSegment StartX=-48 StartY=-6.8 StartZ=0 EndX=-46.3 EndY=-6.8 EndZ=0
    g1: LineSegment StartX=-46.3 StartY=-6.8 StartZ=0 EndX=-46.3 EndY=-12.2 EndZ=0
    g2: LineSegment StartX=-46.3 StartY=-12.2 StartZ=0 EndX=-48 EndY=-12.2 EndZ=0
    g3: LineSegment StartX=-48 StartY=-12.2 StartZ=0 EndX=-48 EndY=-6.8 EndZ=0
  constraints (11):
    c: Coincident(g0,g1)
    c: Coincident(g1,g2)
    c: Coincident(g2,g3)
    c: Coincident(g3,g0)
    c: Horizontal(g0)
    c: Horizontal(g2)
    c: Vertical(g1)
    c: Vertical(g3)
    c: DistanceX(g0,g0) = 1.7
    c: Coincident(g0,g-3)
    c: PointOnObject(g1,g-4)
FEATURE [PartDesign::Pad] Pad008
  BaseFeature = -> Pad007
  Length = 10.6
  Length2 = 100
  Profile = -> Sketch023
  Type = 0
FEATURE [Sketcher::SketchObject] Sketch024
  ExternalGeometry = -> [Pad008]
  MapMode = 5
  Placement = pos=(-48,0,0) rot=(0.57735,-0.57735,-0.57735;2.0944rad)
  Support = -> [Pad008]
  sketch-geometry (1):
    g0: Circle CenterX=-9.5 CenterY=11.2 CenterZ=0 NormalX=0 NormalY=0 NormalZ=1 AngleXU=0 Radius=3
  constraints (3):
    c: Radius(g0) = 3
    c: PointOnObject(g0,g-3)
    c: Distance(g0,g-3) = 2.7
FEATURE [PartDesign::Pocket] Pocket015
  BaseFeature = -> Pad008
  Length = 5
  Length2 = 100
  Profile = -> Sketch024
  Type = 1
FEATURE [Sketcher::SketchObject] Sketch025
  ExternalGeometry = -> [Pocket015]
  MapMode = 5
  Placement = pos=(0,0,21.8) rot=(1,0,0;3.14159rad)
  Support = -> [Pocket015]
  sketch-geometry (4):
    g0: LineSegment StartX=-48 StartY=12.2 StartZ=0 EndX=-46.3 EndY=12.2 EndZ=0
    g1: LineSegment StartX=-46.3 StartY=12.2 StartZ=0 EndX=-46.3 EndY=6.8 EndZ=0
    g2: LineSegment StartX=-46.3 StartY=6.8 StartZ=0 EndX=-48 EndY=6.8 EndZ=0
    g3: LineSegment StartX=-48 StartY=6.8 StartZ=0 EndX=-48 EndY=12.2 EndZ=0
  constraints (11):
    c: Coincident(g0,g1)
    c: Coincident(g1,g2)
    c: Coincident(g2,g3)
    c: Coincident(g3,g0)
    c: Horizontal(g0)
    c: Horizontal(g2)
    c: Vertical(g1)
    c: Vertical(g3)
    c: DistanceX(g2,g2) = 1.7
    c: Coincident(g0,g-3)
    c: PointOnObject(g1,g-4)
FEATURE [PartDesign::Pad] Pad009
  BaseFeature = -> Pocket015
  Length = 10.6
  Length2 = 100
  Profile = -> Sketch025
  Type = 0
FEATURE [Sketcher::SketchObject] Sketch026
  ExternalGeometry = -> [Pad009]
  MapMode = 5
  Placement = pos=(-48,0,0) rot=(0.57735,-0.57735,-0.57735;2.0944rad)
  Support = -> [Pad009]
  sketch-geometry (1):
    g0: Circle CenterX=9.5 CenterY=11.2 CenterZ=0 NormalX=0 NormalY=0 NormalZ=1 AngleXU=0 Radius=3
  constraints (3):
    c: Radius(g0) = 3
    c: PointOnObject(g0,g-3)
    c: Distance(g0,g-3) = 2.7
FEATURE [PartDesign::Pocket] Pocket016
  BaseFeature = -> Pad009
  Length = 5
  Length2 = 100
  Profile = -> Sketch026
  Type = 1
FEATURE [PartDesign::Fillet] Fillet004
  Base = -> Pocket016 [Edge165,Edge155,Edge145,Edge133]
  BaseFeature = -> Pocket016
  Radius = 1
FEATURE [PartDesign::Fillet] Fillet005
  Base = -> Fillet004 [Edge165,Edge168,Edge177,Edge166]
  BaseFeature = -> Fillet004
  Radius = 1
FEATURE [PartDesign::Chamfer] Chamfer001
  Base = -> Fillet005 [Edge51,Edge48,Edge50,Edge49]
  BaseFeature = -> Fillet005
  Size = 1.4
FEATURE [PartDesign::Body] Body001  label="RearCover"
  Group = -> [Sketch016,Pad003,Sketch017,Pad004,Sketch018,Pocket013,Sketch019,Pad005,Sketch020,Pad006,Sketch021,Pocket014,Sketch022,Pad007,Sketch023,Pad008,Sketch024,Pocket015,Sketch025,Pad009,Sketch026,Pocket016,Fillet004,Fillet005,Chamfer001]
  Origin = -> Origin001
  Tip = -> Chamfer001
FEATURE [Sketcher::SketchObject] Sketch027
  AttachmentOffset = pos=(0,0,13.4) rot=(0,0,1;0rad)
  MapMode = 5
  Placement = pos=(0,0,13.4) rot=(0,0,1;0rad)
  Support = -> [XY_Plane002]
  expr: Constraints[11] = -33.5 + 3 + 3.8 / 2
  expr: Constraints[10] = -46.3 + 13.1 + 0.5
  expr: AttachmentOffset.Base.z = 13.1 + Measures.J2
  sketch-geometry (4):
    g0: LineSegment StartX=-32.7 StartY=-28.6 StartZ=0 EndX=-26.7 EndY=-28.6 EndZ=0
    g1: LineSegment StartX=-26.7 StartY=-28.6 StartZ=0 EndX=-26.7 EndY=-32.4 EndZ=0
    g2: LineSegment StartX=-26.7 StartY=-32.4 StartZ=0 EndX=-32.7 EndY=-32.4 EndZ=0
    g3: LineSegment StartX=-32.7 StartY=-32.4 StartZ=0 EndX=-32.7 EndY=-28.6 EndZ=0
  constraints (12):
    c: Coincident(g0,g1)
    c: Coincident(g1,g2)
    c: Coincident(g2,g3)
    c: Coincident(g3,g0)
    c: Horizontal(g0)
    c: Horizontal(g2)
    c: Vertical(g1)
    c: Vertical(g3)
    c: DistanceY(g1,g1) = 3.8
    c: DistanceX(g0,g0) = 6
    c: DistanceX(g-2,g0) = -32.7
    c: DistanceY(g-1,g0) = -28.6
FEATURE [PartDesign::Pad] Pad010
  Length = 2
  Length2 = 100
  Profile = -> Sketch027
  Type = 0
FEATURE [Sketcher::SketchObject] Sketch028
  AttachmentOffset = pos=(0,0,13.4) rot=(0,0,1;0rad)
  MapMode = 5
  Placement = pos=(0,0,13.4) rot=(0,0,1;0rad)
  Support = -> [XY_Plane003]
  expr: Constraints[11] = -32.7 + 15.7
  expr: Constraints[8] = -33.5 + 3 + 3.8 / 2
  expr: AttachmentOffset.Base.z = 13.1 + Measures.J2
  sketch-geometry (4):
    g0: LineSegment StartX=-17 StartY=-28.6 StartZ=0 EndX=-11 EndY=-28.6 EndZ=0
    g1: LineSegment StartX=-11 StartY=-28.6 StartZ=0 EndX=-11 EndY=-32.4 EndZ=0
    g2: LineSegment StartX=-11 StartY=-32.4 StartZ=0 EndX=-17 EndY=-32.4 EndZ=0
    g3: LineSegment StartX=-17 StartY=-32.4 StartZ=0 EndX=-17 EndY=-28.6 EndZ=0
  constraints (12):
    c: Coincident(g0,g1)
    c: Coincident(g1,g2)
    c: Coincident(g2,g3)
    c: Coincident(g3,g0)
    c: Horizontal(g0)
    c: Horizontal(g2)
    c: Vertical(g1)
    c: Vertical(g3)
    c: DistanceY(g-1,g0) = -28.6
    c: DistanceY(g1,g1) = 3.8
    c: DistanceX(g0,g0) = 6
    c: DistanceX(g-2,g0) = -17
FEATURE [PartDesign::Pad] Pad011
  Length = 2
  Length2 = 100
  Profile = -> Sketch028
  Type = 0
FEATURE [Sketcher::SketchObject] Sketch029
  AttachmentOffset = pos=(0,0,13.4) rot=(0,0,1;0rad)
  MapMode = 5
  Placement = pos=(0,0,13.4) rot=(0,0,1;0rad)
  Support = -> [XY_Plane004]
  expr: Constraints[11] = -33.5 + 3 + 3.8 / 2
  expr: Constraints[10] = -17 + 15.7
  expr: AttachmentOffset.Base.z = 13.1 + Measures.J2
  sketch-geometry (4):
    g0: LineSegment StartX=-1.3 StartY=-28.6 StartZ=0 EndX=4.7 EndY=-28.6 EndZ=0
    g1: LineSegment StartX=4.7 StartY=-28.6 StartZ=0 EndX=4.7 EndY=-32.4 EndZ=0
    g2: LineSegment StartX=4.7 StartY=-32.4 StartZ=0 EndX=-1.3 EndY=-32.4 EndZ=0
    g3: LineSegment StartX=-1.3 StartY=-32.4 StartZ=0 EndX=-1.3 EndY=-28.6 EndZ=0
  constraints (12):
    c: Coincident(g0,g1)
    c: Coincident(g1,g2)
    c: Coincident(g2,g3)
    c: Coincident(g3,g0)
    c: Horizontal(g0)
    c: Horizontal(g2)
    c: Vertical(g1)
    c: Vertical(g3)
    c: DistanceY(g1,g1) = 3.8
    c: DistanceX(g0,g0) = 6
    c: DistanceX(g-2,g0) = -1.3
    c: DistanceY(g-1,g0) = -28.6
FEATURE [PartDesign::Pad] Pad012
  Length = 2
  Length2 = 100
  Profile = -> Sketch029
  Type = 0
FEATURE [Sketcher::SketchObject] Sketch030
  AttachmentOffset = pos=(0,0,13.4) rot=(0,0,1;0rad)
  MapMode = 5
  Placement = pos=(0,0,13.4) rot=(0,0,1;0rad)
  Support = -> [XY_Plane005]
  expr: Constraints[11] = -1.3 + 15.7
  expr: Constraints[10] = -33.5 + 3 + 3.8 / 2
  expr: AttachmentOffset.Base.z = 13.1 + Measures.J2
  sketch-geometry (4):
    g0: LineSegment StartX=14.4 StartY=-28.6 StartZ=0 EndX=20.4 EndY=-28.6 EndZ=0
    g1: LineSegment StartX=20.4 StartY=-28.6 StartZ=0 EndX=20.4 EndY=-32.4 EndZ=0
    g2: LineSegment StartX=20.4 StartY=-32.4 StartZ=0 EndX=14.4 EndY=-32.4 EndZ=0
    g3: LineSegment StartX=14.4 StartY=-32.4 StartZ=0 EndX=14.4 EndY=-28.6 EndZ=0
  constraints (12):
    c: Coincident(g0,g1)
    c: Coincident(g1,g2)
    c: Coincident(g2,g3)
    c: Coincident(g3,g0)
    c: Horizontal(g0)
    c: Horizontal(g2)
    c: Vertical(g1)
    c: Vertical(g3)
    c: DistanceY(g1,g1) = 3.8
    c: DistanceX(g0,g0) = 6
    c: DistanceY(g-1,g0) = -28.6
    c: DistanceX(g-2,g0) = 14.4
FEATURE [PartDesign::Pad] Pad013
  Length = 2
  Length2 = 100
  Profile = -> Sketch030
  Type = 0
FEATURE [Sketcher::SketchObject] Sketch031
  ExternalGeometry = -> [Pad010]
  MapMode = 5
  Placement = pos=(0,0,13.4) rot=(1,0,0;3.14159rad)
  Support = -> [Pad010]
  sketch-geometry (1):
    g0: Circle CenterX=-29.7 CenterY=30.5 CenterZ=0 NormalX=0 NormalY=0 NormalZ=1 AngleXU=0 Radius=1.9
  constraints (3):
    c: Radius(g0) = 1.9
    c: Distance(g0,g-4) = 1.9
    c: Distance(g0,g-3) = 3
FEATURE [PartDesign::Pad] Pad014
  BaseFeature = -> Pad010
  Length = 15.4
  Length2 = 100
  Profile = -> Sketch031
  Type = 0
FEATURE [Sketcher::SketchObject] Sketch032
  ExternalGeometry = -> [Pad011]
  MapMode = 5
  Placement = pos=(0,0,13.4) rot=(1,0,0;3.14159rad)
  Support = -> [Pad011]
  sketch-geometry (1):
    g0: Circle CenterX=-14 CenterY=30.5 CenterZ=0 NormalX=0 NormalY=0 NormalZ=1 AngleXU=0 Radius=1.9
  constraints (3):
    c: Radius(g0) = 1.9
    c: Distance(g0,g-4) = 1.9
    c: Distance(g0,g-3) = 3
FEATURE [PartDesign::Pad] Pad015
  BaseFeature = -> Pad011
  Length = 15.4
  Length2 = 100
  Profile = -> Sketch032
  Type = 0
FEATURE [Sketcher::SketchObject] Sketch033
  ExternalGeometry = -> [Pad012]
  MapMode = 5
  Placement = pos=(0,0,13.4) rot=(1,0,0;3.14159rad)
  Support = -> [Pad012]
  sketch-geometry (1):
    g0: Circle CenterX=1.7 CenterY=30.5 CenterZ=0 NormalX=0 NormalY=0 NormalZ=1 AngleXU=0 Radius=1.9
  constraints (3):
    c: Radius(g0) = 1.9
    c: Distance(g0,g-4) = 1.9
    c: Distance(g0,g-3) = 3
FEATURE [PartDesign::Pad] Pad016
  BaseFeature = -> Pad012
  Length = 15.4
  Length2 = 100
  Profile = -> Sketch033
  Type = 0
FEATURE [Sketcher::SketchObject] Sketch034
  ExternalGeometry = -> [Pad013]
  MapMode = 5
  Placement = pos=(0,0,13.4) rot=(1,0,0;3.14159rad)
  Support = -> [Pad013]
  sketch-geometry (1):
    g0: Circle CenterX=17.4 CenterY=30.5 CenterZ=0 NormalX=0 NormalY=0 NormalZ=1 AngleXU=0 Radius=1.9
  constraints (3):
    c: Radius(g0) = 1.9
    c: Distance(g0,g-4) = 1.9
    c: Distance(g0,g-3) = 3
FEATURE [PartDesign::Pad] Pad017
  BaseFeature = -> Pad013
  Length = 15.4
  Length2 = 100
  Profile = -> Sketch034
  Type = 0
FEATURE [PartDesign::Fillet] Fillet010
  Base = -> Pad014 [Edge19]
  BaseFeature = -> Pad014
  Radius = 1
FEATURE [PartDesign::Body] Body002  label="Pushbutton4"
  Group = -> [Sketch027,Pad010,Sketch031,Pad014,Fillet010]
  Origin = -> Origin002
  Tip = -> Fillet010
FEATURE [PartDesign::Fillet] Fillet011
  Base = -> Pad015 [Edge19]
  BaseFeature = -> Pad015
  Radius = 1
FEATURE [PartDesign::Body] Body003  label="Pushbutton3"
  Group = -> [Sketch028,Pad011,Sketch032,Pad015,Fillet011]
  Origin = -> Origin003
  Tip = -> Fillet011
FEATURE [PartDesign::Fillet] Fillet012
  Base = -> Pad016 [Edge19]
  BaseFeature = -> Pad016
  Radius = 1
FEATURE [PartDesign::Body] Body004  label="Pushbutton2"
  Group = -> [Sketch029,Pad012,Sketch033,Pad016,Fillet012]
  Origin = -> Origin004
  Tip = -> Fillet012
FEATURE [PartDesign::Fillet] Fillet013
  Base = -> Pad017 [Edge19]
  BaseFeature = -> Pad017
  Radius = 1
FEATURE [PartDesign::Body] Body005  label="Pushbutton1"
  Group = -> [Sketch030,Pad013,Sketch034,Pad017,Fillet013]
  Origin = -> Origin005
  Tip = -> Fillet013
FEATURE [Mesh::Feature] Mesh001  label="RearCover (Meshed)"
FEATURE [Mesh::Feature] Mesh002  label="Pushbutton (Meshed)"
FEATURE [Mesh::Feature] Mesh  label="Housing (Meshed)"
